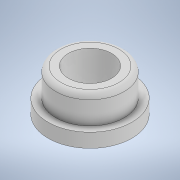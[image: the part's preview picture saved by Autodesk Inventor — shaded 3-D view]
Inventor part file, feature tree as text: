
AUTODESK INVENTOR PART (.ipt)
format: ipt  version: 2022 (Build 260153000, 153)  size: 128,000 bytes
history: native  units: mm
features: extrude x2, sketch x2, fillet x1, projected_geometry x1
ambient origin geometry x8: Origin, YZ Plane, XZ Plane, XY Plane, X Axis, Y Axis, Z Axis, Center Point
bodies: Solid1 (feature_tree)
feature tree (6):
  extrude  "Extrusion1"  Depth=6.2mm
  extrude  "Extrusion2"  Depth=0.75mm
  fillet  "Fillet1"  Radius=2.0mm
  sketch  "Sketch1"  dims[d0=9.8mm d1=6.2mm]
  sketch  "Sketch2"  dims[d2=6.0mm d3=0.0mm d4=12.0mm d5=2.0mm d6=0.0mm d7=0.75mm]
  projected_geometry  "Projected Loop1"
